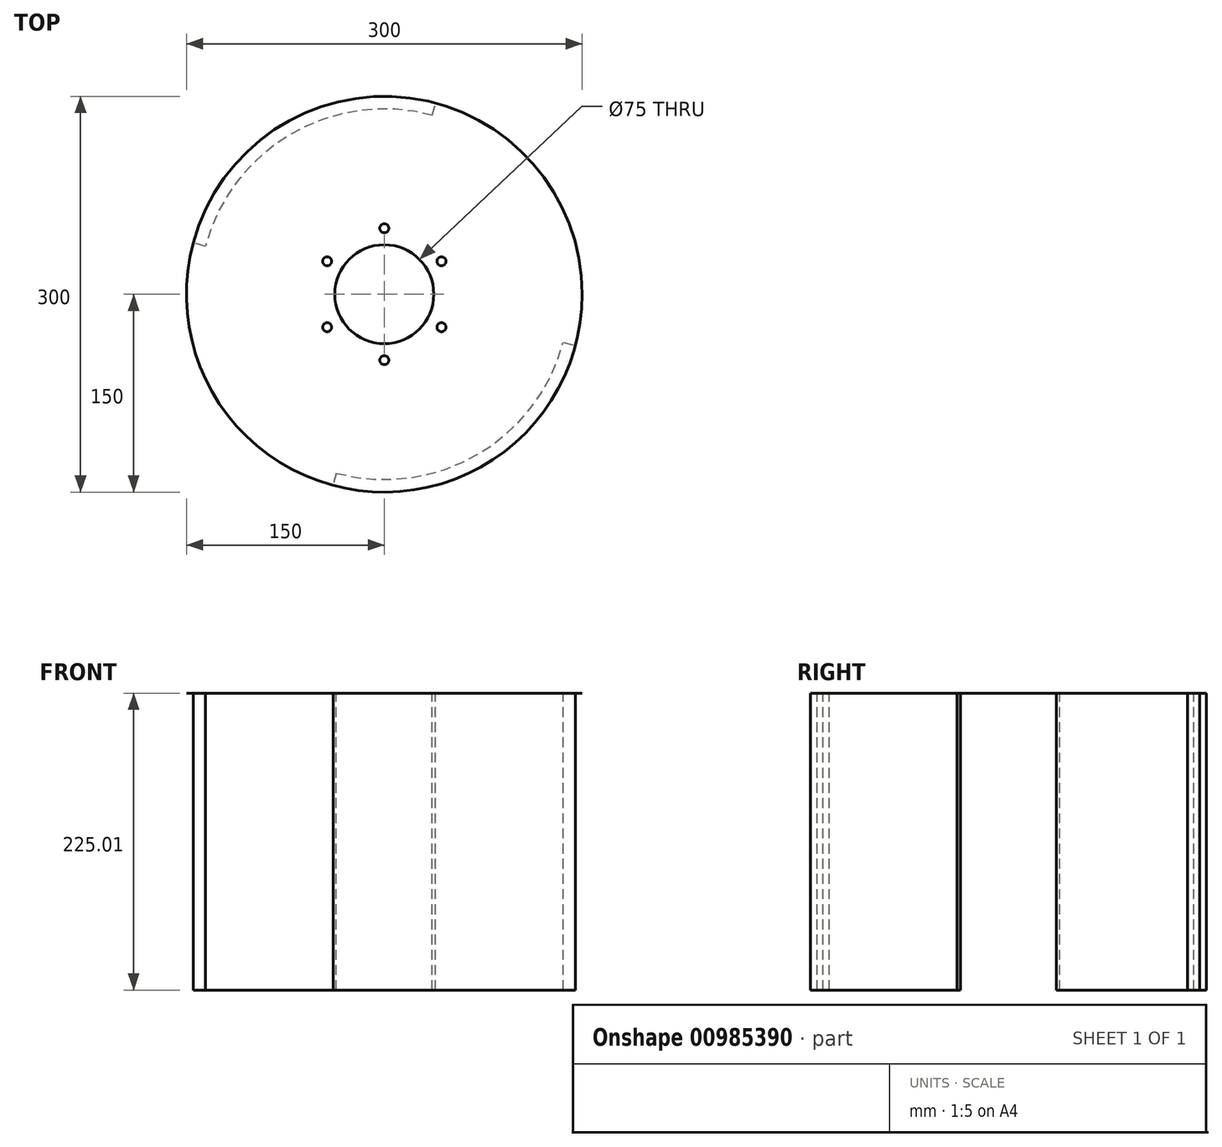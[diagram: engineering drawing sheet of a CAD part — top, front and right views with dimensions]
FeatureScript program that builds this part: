
annotation { "Feature Type Name" : "Feature", "Feature Type Description" : "" }
export const myFeature = defineFeature(function(context is Context, id is Id, definition is map)
    precondition{}
    {
        {
            var Q0;
            Q0=qCreatedBy(makeId("Top.planeOp"),FACE);
            var sketch = newSketch(context, id + "F0", { "sketchPlane" : qUnion([Q0])});
            skCircle(sketch, "E0", {"center": v(0, 0) * mm, "radius": 150 * mm});
            skCircle(sketch, "E1.0", {"center": v(0, 50) * mm, "radius": 3.4 * mm});
            skCircle(sketch, "E2.0", {"center": v(43.3, 25) * mm, "radius": 3.4 * mm});
            skCircle(sketch, "E3.0", {"center": v(43.3, -25) * mm, "radius": 3.4 * mm});
            skCircle(sketch, "E4.0", {"center": v(0, -50) * mm, "radius": 3.4 * mm});
            skCircle(sketch, "E4.1", {"center": v(-43.3, -25) * mm, "radius": 3.4 * mm});
            skCircle(sketch, "E4.2", {"center": v(-43.3, 25) * mm, "radius": 3.4 * mm});
            skCircle(sketch, "E5.0", {"center": v(0, 0) * mm, "radius": 37.5 * mm});
            skCircle(sketch, "E6", {"center": v(0, 0) * mm, "radius": 50 * mm, "construction": true});
            skSolve(sketch);
        }
        {
            var Q0;
            Q0 = qSketchRegion(id + "F0", true);
            extrude(context, id + "F1", {"entities" : qUnion([Q0]), "depth" : 3 / 203.2 * mm, "offsetDistance" : 25 * mm});
        }
        {
            var Q0;
            Q0=makeQuery(id+"F1.opExtrude","CAP_FACE",FACE,{"disambiguationData":[OSD([sQuery(id+"F0.wireOp",EDGE,"E0"),sQuery(id+"F0.wireOp",EDGE,"E1.0"),sQuery(id+"F0.wireOp",EDGE,"E2.0"),sQuery(id+"F0.wireOp",EDGE,"E3.0"),sQuery(id+"F0.wireOp",EDGE,"E4.0"),sQuery(id+"F0.wireOp",EDGE,"E4.1"),sQuery(id+"F0.wireOp",EDGE,"E4.2"),sQuery(id+"F0.wireOp",EDGE,"E5.0")])],"isStart":true});
            var sketch = newSketch(context, id + "F2", { "sketchPlane" : qUnion([Q0])});
            skArc(sketch, "E7.0", {"start": v(-144.89, -38.82) * mm, "mid": v(-75, -129.9) * mm, "end": v(38.82, -144.89) * mm});
            skArc(sketch, "E8.0", {"start": v(-135.69, -36.36) * mm, "mid": v(-70.24, -121.65) * mm, "end": v(36.36, -135.69) * mm});
            skLineSegment(sketch, "E9", {"start": v(0, 0) * mm, "end": v(178.84, -103.25) * mm, "construction": true});
            skLineSegment(sketch, "E10", {"start": v(135.69, 36.36) * mm, "end": v(144.89, 38.82) * mm});
            skLineSegment(sketch, "E11", {"start": v(-36.36, 135.69) * mm, "end": v(-38.82, 144.89) * mm});
            skLineSegment(sketch, "E12", {"start": v(0, 0) * mm, "end": v(-168.26, 97.15) * mm, "construction": true});
            skArc(sketch, "E13.trimOffspring", {"start": v(144.89, 38.82) * mm, "mid": v(75, 129.9) * mm, "end": v(-38.82, 144.89) * mm});
            skArc(sketch, "E14.trimOffspring", {"start": v(135.69, 36.36) * mm, "mid": v(70.24, 121.65) * mm, "end": v(-36.36, 135.69) * mm});
            skLineSegment(sketch, "E15", {"start": v(-135.69, -36.36) * mm, "end": v(-144.89, -38.82) * mm});
            skLineSegment(sketch, "E16", {"start": v(36.36, -135.69) * mm, "end": v(38.82, -144.89) * mm});
            skSolve(sketch);
        }
        {
            var Q0;
            Q0 = qSketchRegion(id + "F2", true);
            extrude(context, id + "F3", {"entities" : qUnion([Q0]), "operationType" : NewBodyOperationType.ADD, "depth" : 300 * mm - 75 * mm, "offsetDistance" : 25 * mm});
        }
    });
